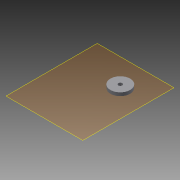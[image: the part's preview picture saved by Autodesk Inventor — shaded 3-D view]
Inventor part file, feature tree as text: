
AUTODESK INVENTOR PART (.ipt)
format: ipt  version: 2014 (Build 180170000, 170)  size: 98,816 bytes
history: native  units: mm
features: plane x1, extrude x1, sketch x1, reference x1
ambient origin geometry x8: Origin, YZ Plane, XZ Plane, XY Plane, X Axis, Y Axis, Z Axis, Center Point
bodies: 实体1 (feature_tree)
feature tree (4):
  plane  "工作平面1"
  extrude  "拉伸1"  Depth=5.0mm TaperAngle=0.0deg
  sketch  "草图2"  dims[d0=30.0mm d1=5.0mm d2=0.0mm]
  reference  "参考1"
